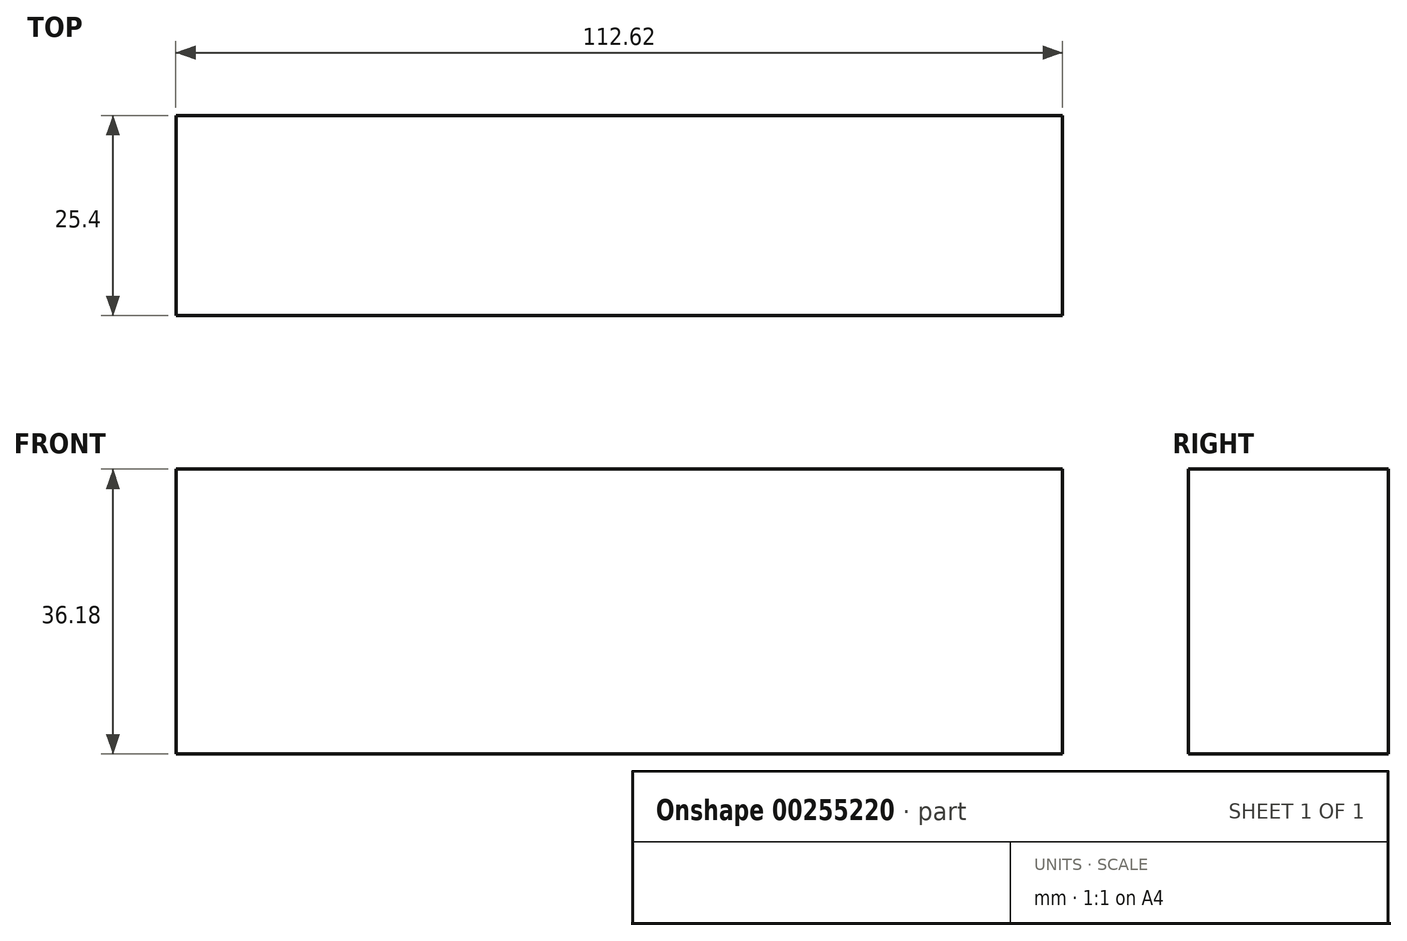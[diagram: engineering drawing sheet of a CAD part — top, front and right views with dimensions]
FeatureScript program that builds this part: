
annotation { "Feature Type Name" : "Feature", "Feature Type Description" : "" }
export const myFeature = defineFeature(function(context is Context, id is Id, definition is map)
    precondition{}
    {
        {
            var Q0;
            Q0=qCreatedBy(makeId("Front.planeOp"),FACE);
            var sketch = newSketch(context, id + "F0", { "sketchPlane" : qUnion([Q0])});
            skLineSegment(sketch, "E0.bottom", {"start": v(-56.3, 18.1) * mm, "end": v(56.3, 18.1) * mm});
            skLineSegment(sketch, "E0.top", {"start": v(-56.3, -18.1) * mm, "end": v(56.3, -18.1) * mm});
            skLineSegment(sketch, "E0.left", {"start": v(-56.3, 18.1) * mm, "end": v(-56.3, -18.1) * mm});
            skLineSegment(sketch, "E0.right", {"start": v(56.3, 18.1) * mm, "end": v(56.3, -18.1) * mm});
            skPoint(sketch, "E0.middle", {"position": v(0, 0) * mm});
            skLineSegment(sketch, "E1", {"start": v(56.3, -10.93) * mm, "end": v(56.3, 15.97) * mm});
            skSolve(sketch);
        }
        {
            var Q0;
            {var subQ1=sQuery(id+"F0.wireOp",EDGE,"E0.bottom");Q0=makeQuery(id+"F0.imprint","IMPRINT",FACE,{"disambiguationData":[TD([[makeQuery(id+"F0.imprint","IMPRINT",EDGE,{"derivedFrom":subQ1}),-1.0]])]});}
            extrude(context, id + "F1", {"entities" : qUnion([Q0]), "depth" : 25.4 * mm});
        }
    });
